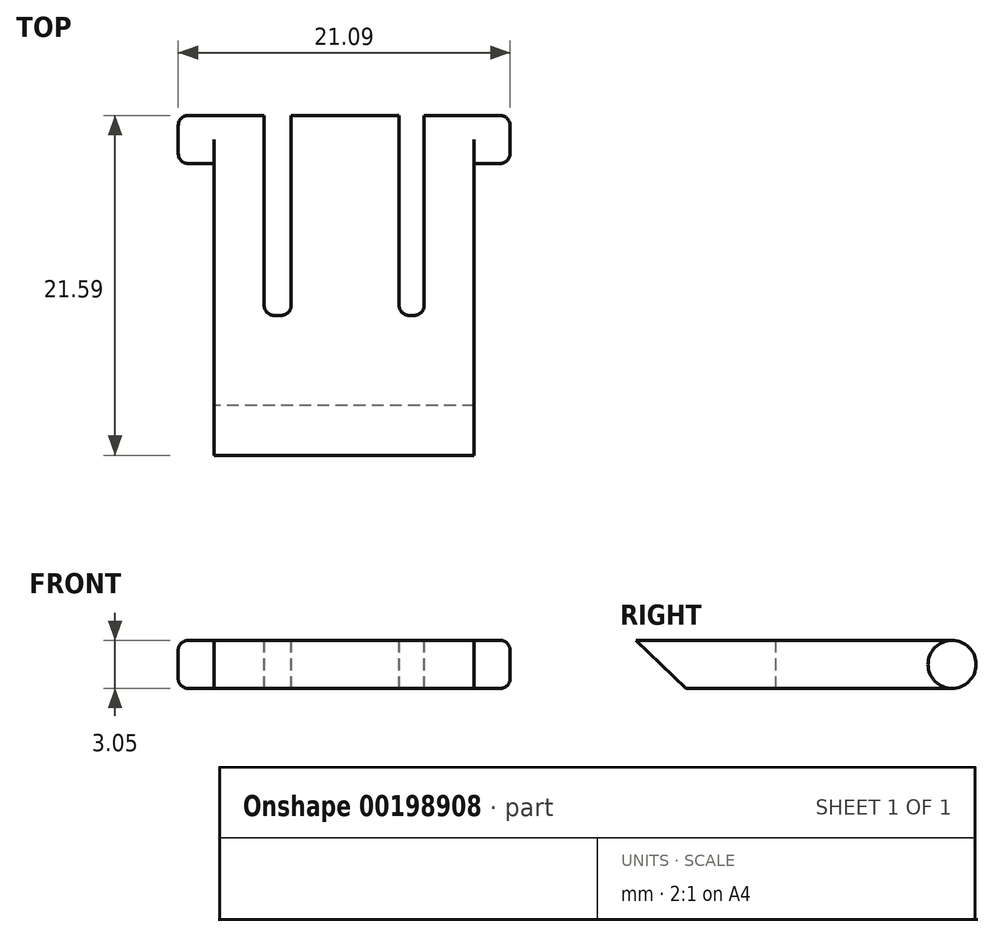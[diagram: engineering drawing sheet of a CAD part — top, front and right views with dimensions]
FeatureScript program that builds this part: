
annotation { "Feature Type Name" : "Feature", "Feature Type Description" : "" }
export const myFeature = defineFeature(function(context is Context, id is Id, definition is map)
    precondition{}
    {
        {
            var Q0;
            Q0=qCreatedBy(makeId("Top.planeOp"),FACE);
            var sketch = newSketch(context, id + "F0", { "sketchPlane" : qUnion([Q0])});
            skLineSegment(sketch, "E0.bottom", {"start": v(0, 0) * mm, "end": v(16.51, 0) * mm});
            skLineSegment(sketch, "E0.top", {"start": v(0, 21.59) * mm, "end": v(16.51, 21.59) * mm});
            skLineSegment(sketch, "E0.left", {"start": v(0, 0) * mm, "end": v(0, 21.59) * mm});
            skLineSegment(sketch, "E0.right", {"start": v(16.51, 0) * mm, "end": v(16.51, 21.59) * mm});
            skSolve(sketch);
        }
        {
            var Q0;
            Q0 = qSketchRegion(id + "F0", true);
            extrude(context, id + "F1", {"entities" : qUnion([Q0]), "depth" : 3.05 * mm});
        }
        {
            var Q0;
            Q0=makeQuery(id+"F1.opExtrude","CAP_FACE",FACE,{"disambiguationData":[OSD([sQuery(id+"F0.wireOp",EDGE,"E0.bottom"),sQuery(id+"F0.wireOp",EDGE,"E0.top"),sQuery(id+"F0.wireOp",EDGE,"E0.left"),sQuery(id+"F0.wireOp",EDGE,"E0.right")])],"isStart":false});
            var sketch = newSketch(context, id + "F2", { "sketchPlane" : qUnion([Q0])});
            skLineSegment(sketch, "E1.bottom", {"start": v(3.17, 21.59) * mm, "end": v(4.89, 21.59) * mm});
            skLineSegment(sketch, "E1.top", {"start": v(3.18, 8.9) * mm, "end": v(4.89, 8.9) * mm});
            skLineSegment(sketch, "E1.left", {"start": v(3.17, 21.59) * mm, "end": v(3.18, 8.9) * mm});
            skLineSegment(sketch, "E1.right", {"start": v(4.89, 21.59) * mm, "end": v(4.89, 8.9) * mm});
            skSolve(sketch);
        }
        {
            var Q0;
            Q0 = qSketchRegion(id + "F2", true);
            extrude(context, id + "F3", {"entities" : qUnion([Q0]), "operationType" : NewBodyOperationType.REMOVE, "oppositeDirection" : true, "depth" : 25.4 * mm});
        }
        {
            var Q0;
            Q0=makeQuery(id+"F1.opExtrude","CAP_FACE",FACE,{"disambiguationData":[OSD([sQuery(id+"F0.wireOp",EDGE,"E0.bottom"),sQuery(id+"F0.wireOp",EDGE,"E0.top"),sQuery(id+"F0.wireOp",EDGE,"E0.left"),sQuery(id+"F0.wireOp",EDGE,"E0.right")])],"isStart":false});
            var sketch = newSketch(context, id + "F4", { "sketchPlane" : qUnion([Q0])});
            skLineSegment(sketch, "E2.bottom", {"start": v(11.75, 21.59) * mm, "end": v(13.34, 21.59) * mm});
            skLineSegment(sketch, "E2.top", {"start": v(11.75, 8.9) * mm, "end": v(13.34, 8.9) * mm});
            skLineSegment(sketch, "E2.left", {"start": v(11.75, 21.59) * mm, "end": v(11.75, 8.9) * mm});
            skLineSegment(sketch, "E2.right", {"start": v(13.34, 21.59) * mm, "end": v(13.34, 8.9) * mm});
            skSolve(sketch);
        }
        {
            var Q0;
            Q0=makeQuery(id+"F4.imprint","IMPRINT",FACE,{"disambiguationData":[TD([[makeQuery(id+"F4.imprint","IMPRINT",EDGE,{"derivedFrom":sQuery(id+"F4.wireOp",EDGE,"E2.bottom")}),-1.0]])]});
            extrude(context, id + "F5", {"entities" : qUnion([Q0]), "operationType" : NewBodyOperationType.REMOVE, "oppositeDirection" : true, "depth" : 25.4 * mm});
        }
        {
            var Q0;
            Q0=makeQuery(id+"F1.opExtrude","SWEPT_FACE",FACE,{"disambiguationData":[OSD([sQuery(id+"F0.wireOp",EDGE,"E0.left")])]});
            var sketch = newSketch(context, id + "F6", { "sketchPlane" : qUnion([Q0])});
            skLineSegment(sketch, "E3", {"start": v(0, 3.05) * mm, "end": v(-3.17, 0) * mm});
            skLineSegment(sketch, "E4", {"start": v(-3.18, 0) * mm, "end": v(0, 0) * mm});
            skLineSegment(sketch, "E5", {"start": v(0, 0) * mm, "end": v(0, 3.05) * mm});
            skSolve(sketch);
        }
        {
            var Q0;
            Q0=makeQuery(id+"F6.imprint","IMPRINT",FACE,{"disambiguationData":[TD([[makeQuery(id+"F6.imprint","IMPRINT",EDGE,{"derivedFrom":sQuery(id+"F6.wireOp",EDGE,"E3")}),1.0]])]});
            extrude(context, id + "F7", {"entities" : qUnion([Q0]), "operationType" : NewBodyOperationType.REMOVE, "oppositeDirection" : true, "depth" : 25.4 * mm});
        }
        {
            var Q0;
            {var subQ0=sQuery(id+"F0.wireOp",EDGE,"E0.left");var subQ1=sQuery(id+"F0.wireOp",EDGE,"E0.top");Q0=makeQuery(id+"F3.boolean.opBoolean","SPLIT",EDGE,{"disambiguationData":[TD([makeQuery(id+"F1.opExtrude","SWEPT_FACE",FACE,{"disambiguationData":[OSD([subQ0])]})])],"derivedFrom":makeQuery(id+"F1.opExtrude","CAP_EDGE",EDGE,{"disambiguationData":[OSD([subQ1])],"isStart":false})});}
            var Q1;
            {var subQ0=sQuery(id+"F0.wireOp",EDGE,"E0.left");var subQ1=sQuery(id+"F0.wireOp",EDGE,"E0.top");Q1=makeQuery(id+"F3.boolean.opBoolean","SPLIT",EDGE,{"disambiguationData":[TD([makeQuery(id+"F1.opExtrude","SWEPT_FACE",FACE,{"disambiguationData":[OSD([subQ0])]})])],"derivedFrom":makeQuery(id+"F1.opExtrude","CAP_EDGE",EDGE,{"disambiguationData":[OSD([subQ1])],"isStart":true})});}
            var Q2;
            {var subQ0=sQuery(id+"F0.wireOp",EDGE,"E0.right");var subQ1=sQuery(id+"F0.wireOp",EDGE,"E0.top");var subQ4=makeQuery(id+"F3.opExtrude","SWEPT_FACE",FACE,{"disambiguationData":[OSD([sQuery(id+"F2.wireOp",EDGE,"E1.right")])]});Q2=makeQuery(id+"F5.boolean.opBoolean","SPLIT",EDGE,{"disambiguationData":[TD([makeQuery(id+"F3.boolean.opBoolean","COPY",FACE,{"derivedFrom":subQ4})])],"derivedFrom":makeQuery(id+"F3.boolean.opBoolean","SPLIT",EDGE,{"disambiguationData":[TD([makeQuery(id+"F1.opExtrude","SWEPT_FACE",FACE,{"disambiguationData":[OSD([subQ0])]})])],"derivedFrom":makeQuery(id+"F1.opExtrude","CAP_EDGE",EDGE,{"disambiguationData":[OSD([subQ1])],"isStart":false})})});}
            var Q3;
            {var subQ0=sQuery(id+"F0.wireOp",EDGE,"E0.right");var subQ1=sQuery(id+"F0.wireOp",EDGE,"E0.top");var subQ4=makeQuery(id+"F3.opExtrude","SWEPT_FACE",FACE,{"disambiguationData":[OSD([sQuery(id+"F2.wireOp",EDGE,"E1.right")])]});Q3=makeQuery(id+"F5.boolean.opBoolean","SPLIT",EDGE,{"disambiguationData":[TD([makeQuery(id+"F3.boolean.opBoolean","COPY",FACE,{"derivedFrom":subQ4})])],"derivedFrom":makeQuery(id+"F3.boolean.opBoolean","SPLIT",EDGE,{"disambiguationData":[TD([makeQuery(id+"F1.opExtrude","SWEPT_FACE",FACE,{"disambiguationData":[OSD([subQ0])]})])],"derivedFrom":makeQuery(id+"F1.opExtrude","CAP_EDGE",EDGE,{"disambiguationData":[OSD([subQ1])],"isStart":true})})});}
            var Q4;
            {var subQ0=sQuery(id+"F0.wireOp",EDGE,"E0.right");var subQ1=sQuery(id+"F0.wireOp",EDGE,"E0.top");var subQ4=makeQuery(id+"F1.opExtrude","SWEPT_FACE",FACE,{"disambiguationData":[OSD([subQ0])]});Q4=makeQuery(id+"F5.boolean.opBoolean","SPLIT",EDGE,{"disambiguationData":[TD([subQ4])],"derivedFrom":makeQuery(id+"F3.boolean.opBoolean","SPLIT",EDGE,{"disambiguationData":[TD([subQ4])],"derivedFrom":makeQuery(id+"F1.opExtrude","CAP_EDGE",EDGE,{"disambiguationData":[OSD([subQ1])],"isStart":false})})});}
            var Q5;
            {var subQ0=sQuery(id+"F0.wireOp",EDGE,"E0.right");var subQ1=sQuery(id+"F0.wireOp",EDGE,"E0.top");var subQ4=makeQuery(id+"F1.opExtrude","SWEPT_FACE",FACE,{"disambiguationData":[OSD([subQ0])]});Q5=makeQuery(id+"F5.boolean.opBoolean","SPLIT",EDGE,{"disambiguationData":[TD([subQ4])],"derivedFrom":makeQuery(id+"F3.boolean.opBoolean","SPLIT",EDGE,{"disambiguationData":[TD([subQ4])],"derivedFrom":makeQuery(id+"F1.opExtrude","CAP_EDGE",EDGE,{"disambiguationData":[OSD([subQ1])],"isStart":true})})});}
            fillet(context, id + "F8", {"entities" : qUnion([Q0, Q1, Q2, Q3, Q4, Q5]), "radius" : 1.52 * mm, "tangentPropagation" : true, "allowEdgeOverflow" : false});
        }
        {
            var Q0;
            Q0=makeQuery(id+"F1.opExtrude","SWEPT_FACE",FACE,{"disambiguationData":[OSD([sQuery(id+"F0.wireOp",EDGE,"E0.left")])]});
            var sketch = newSketch(context, id + "F9", { "sketchPlane" : qUnion([Q0])});
            skCircle(sketch, "E6", {"center": v(-20.07, 1.52) * mm, "radius": 1.52 * mm});
            skSolve(sketch);
        }
        {
            var Q0;
            Q0 = qSketchRegion(id + "F9", true);
            extrude(context, id + "F10", {"entities" : qUnion([Q0]), "operationType" : NewBodyOperationType.ADD, "depth" : 2.3 * mm});
        }
        {
            var Q0;
            Q0=makeQuery(id+"F1.opExtrude","SWEPT_FACE",FACE,{"disambiguationData":[OSD([sQuery(id+"F0.wireOp",EDGE,"E0.right")])]});
            var sketch = newSketch(context, id + "F11", { "sketchPlane" : qUnion([Q0])});
            skCircle(sketch, "E7", {"center": v(20.07, 1.52) * mm, "radius": 1.52 * mm});
            skSolve(sketch);
        }
        {
            var Q0;
            Q0 = qSketchRegion(id + "F11", true);
            extrude(context, id + "F12", {"entities" : qUnion([Q0]), "operationType" : NewBodyOperationType.ADD, "depth" : 2.3 * mm});
        }
        {
            var Q0;
            Q0=makeQuery(id+"F12.opExtrude","CAP_EDGE",EDGE,{"disambiguationData":[OSD([sQuery(id+"F11.wireOp",EDGE,"E7")])],"isStart":false});
            var Q1;
            Q1=makeQuery(id+"F10.opExtrude","CAP_EDGE",EDGE,{"disambiguationData":[OSD([sQuery(id+"F9.wireOp",EDGE,"E6")])],"isStart":false});
            fillet(context, id + "F13", {"entities" : qUnion([Q0, Q1]), "radius" : 0.64 * mm, "tangentPropagation" : true, "allowEdgeOverflow" : false});
        }
        {
            var Q0;
            Q0=makeQuery(id+"F5.boolean.opBoolean","COPY",EDGE,{"derivedFrom":makeQuery(id+"F5.opExtrude","SWEPT_EDGE",EDGE,{"disambiguationData":[OSD([sQuery(id+"F4.wireOp",EDGE,"E2.top"),sQuery(id+"F4.wireOp",EDGE,"E2.left")])]})});
            var Q1;
            Q1=makeQuery(id+"F5.boolean.opBoolean","COPY",EDGE,{"derivedFrom":makeQuery(id+"F5.opExtrude","SWEPT_EDGE",EDGE,{"disambiguationData":[OSD([sQuery(id+"F4.wireOp",EDGE,"E2.top"),sQuery(id+"F4.wireOp",EDGE,"E2.right")])]})});
            var Q2;
            Q2=makeQuery(id+"F3.boolean.opBoolean","COPY",EDGE,{"derivedFrom":makeQuery(id+"F3.opExtrude","SWEPT_EDGE",EDGE,{"disambiguationData":[OSD([sQuery(id+"F2.wireOp",EDGE,"E1.top"),sQuery(id+"F2.wireOp",EDGE,"E1.left")])]})});
            var Q3;
            Q3=makeQuery(id+"F3.boolean.opBoolean","COPY",EDGE,{"derivedFrom":makeQuery(id+"F3.opExtrude","SWEPT_EDGE",EDGE,{"disambiguationData":[OSD([sQuery(id+"F2.wireOp",EDGE,"E1.top"),sQuery(id+"F2.wireOp",EDGE,"E1.right")])]})});
            fillet(context, id + "F14", {"entities" : qUnion([Q0, Q1, Q2, Q3]), "radius" : 0.64 * mm, "tangentPropagation" : true, "allowEdgeOverflow" : false});
        }
    });
